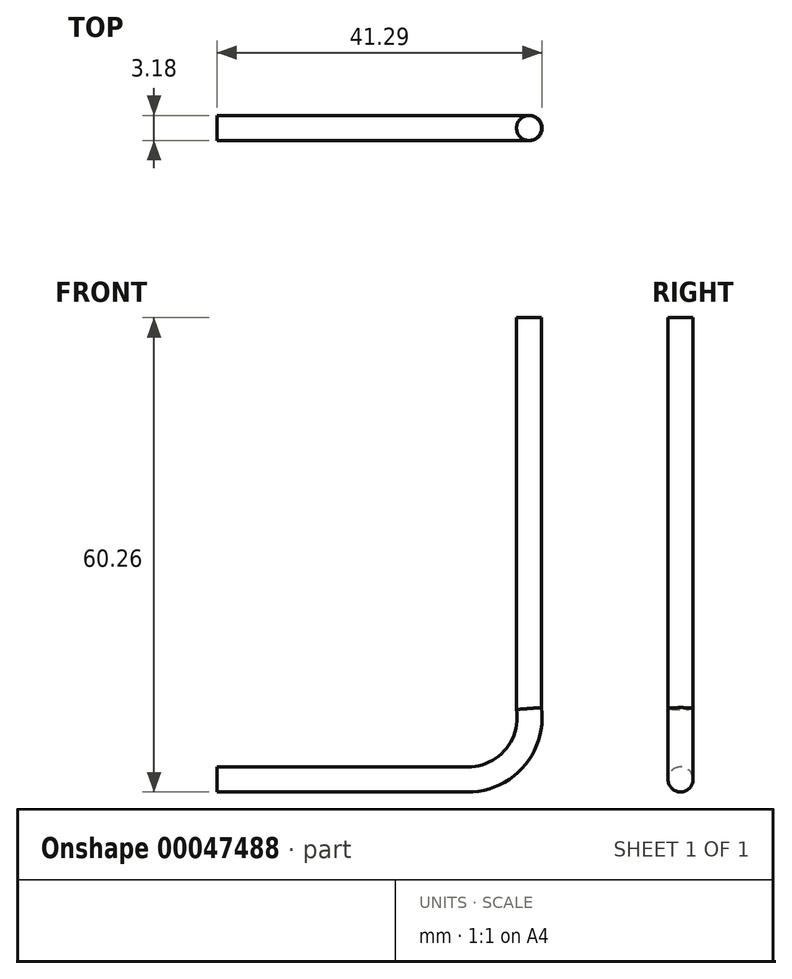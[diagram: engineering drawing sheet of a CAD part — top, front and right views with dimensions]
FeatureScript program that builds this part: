
annotation { "Feature Type Name" : "Feature", "Feature Type Description" : "" }
export const myFeature = defineFeature(function(context is Context, id is Id, definition is map)
    precondition{}
    {
        {
            var Q0;
            Q0=qCreatedBy(makeId("Front.planeOp"),FACE);
            var sketch = newSketch(context, id + "F0", { "sketchPlane" : qUnion([Q0])});
            skLineSegment(sketch, "E0", {"start": v(0, 0) * mm, "end": v(31.83, 0) * mm});
            skArc(sketch, "E1", {"start": v(31.83, 0) * mm, "mid": v(37.8, 2.73) * mm, "end": v(39.62, 9.02) * mm});
            skLineSegment(sketch, "E2", {"start": v(39.62, 9.02) * mm, "end": v(39.62, 58.67) * mm});
            skSolve(sketch);
        }
        {
            var Q0;
            Q0=qCreatedBy(makeId("Right.planeOp"),FACE);
            var sketch = newSketch(context, id + "F1", { "sketchPlane" : qUnion([Q0])});
            skCircle(sketch, "E3", {"center": v(0, 0) * mm, "radius": 1.59 * mm});
            skSolve(sketch);
        }
        {
            var Q0;
            Q0 = qSketchRegion(id + "F1", true);
            var Q1;
            Q1 = qConstructionFilter(qBodyType(qCreatedBy(id + "F0" ,EDGE), BodyType.WIRE), ConstructionObject.NO);
            sweep(context, id + "F2", {"profiles" : qUnion([Q0]), "path" : qUnion([Q1])});
        }
    });
